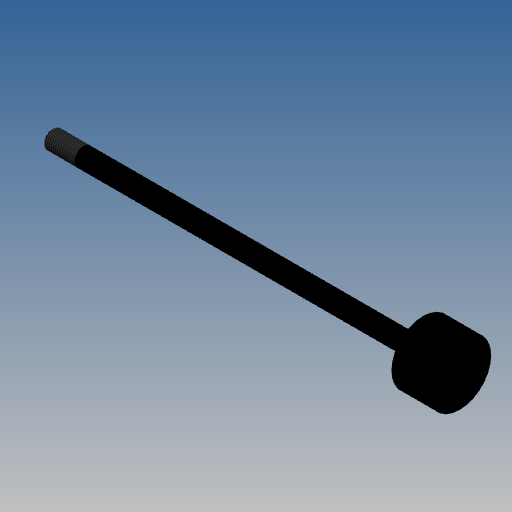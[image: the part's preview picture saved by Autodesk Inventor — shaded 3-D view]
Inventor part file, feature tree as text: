
AUTODESK INVENTOR PART (.ipt)
format: ipt  version: 2020 (Build 240168000, 168)  size: 157,184 bytes
history: native  units: in
note: dims shown in document units (in); Inventor stores cm internally (conversion verified against a paired STEP export)
features: other x98, sketch x3, revolve x2, thread x1, extrude x1
ambient origin geometry x8: Origin, YZ Plane, XZ Plane, XY Plane, X Axis, Y Axis, Z Axis, Center Point
bodies: Solid1 (feature_tree)
feature tree (105):
  revolve  "Revolution1"  Angle=360.0deg
  revolve  "Revolution2"  [1 undecoded]
  thread  "Thread1"  [1 undecoded]
  extrude  "Extrusion1"  [1 undecoded]
  other  "dia1_XY"
  other  "dia1_YZ"
  other  "dia1_ZX"
  other  "dia1_X"
  other  "dia1_Y"
  other  "dia1_Z"
  other  "dia1_Center"
  other  "dia12_XY"
  other  "dia12_YZ"
  other  "dia12_ZX"
  other  "dia12_X"
  other  "dia12_Y"
  other  "dia12_Z"
  other  "dia12_Center"
  other  "dia2_XY"
  other  "dia2_YZ"
  other  "dia2_ZX"
  other  "dia2_X"
  other  "dia2_Y"
  other  "dia2_Z"
  other  "dia2_Center"
  other  "dia22_XY"
  other  "dia22_YZ"
  other  "dia22_ZX"
  other  "dia22_X"
  other  "dia22_Y"
  other  "dia22_Z"
  other  "dia22_Center"
  other  "rl1_XY"
  other  "rl1_YZ"
  other  "rl1_ZX"
  other  "rl1_X"
  other  "rl1_Y"
  other  "rl1_Z"
  other  "rl1_Center"
  other  "rl2_XY"
  other  "rl2_YZ"
  other  "rl2_ZX"
  other  "rl2_X"
  other  "rl2_Y"
  other  "rl2_Z"
  other  "rl2_Center"
  other  "rod_cp_XY"
  other  "rod_cp_YZ"
  other  "rod_cp_ZX"
  other  "rod_cp_X"
  other  "rod_cp_Y"
  other  "rod_cp_Z"
  other  "rod_cp_Center"
  other  "thd1_XY"
  other  "thd1_YZ"
  other  "thd1_ZX"
  other  "thd1_X"
  other  "thd1_Y"
  other  "thd1_Z"
  other  "thd1_Center"
  other  "thd2_XY"
  other  "thd2_YZ"
  other  "thd2_ZX"
  other  "thd2_X"
  other  "thd2_Y"
  other  "thd2_Z"
  other  "thd2_Center"
  other  "to_rod_clevis_XY"
  other  "to_rod_clevis_YZ"
  other  "to_rod_clevis_ZX"
  other  "to_rod_clevis_X"
  other  "to_rod_clevis_Y"
  other  "to_rod_clevis_Z"
  other  "to_rod_clevis_Center"
  other  "wf1_XY"
  other  "wf1_YZ"
  other  "wf1_ZX"
  other  "wf1_X"
  other  "wf1_Y"
  other  "wf1_Z"
  other  "wf1_Center"
  other  "wf2_XY"
  other  "wf2_YZ"
  other  "wf2_ZX"
  other  "wf2_X"
  other  "wf2_Y"
  other  "wf2_Z"
  other  "wf2_Center"
  other  "wfw1_XY"
  other  "wfw1_YZ"
  other  "wfw1_ZX"
  other  "wfw1_X"
  other  "wfw1_Y"
  other  "wfw1_Z"
  other  "wfw1_Center"
  other  "wfw2_XY"
  other  "wfw2_YZ"
  other  "wfw2_ZX"
  other  "wfw2_X"
  other  "wfw2_Y"
  other  "wfw2_Z"
  other  "wfw2_Center"
  sketch  "Sketch_1"  dims[d0=360.0deg d1=360.0deg]
  sketch  "Sketch_3"  dims[d2=0.7203in d3=0.0in d4=0.25in d5=0.0in]
  sketch  "Sketch_10"  dims[d6=0.0in d7=0.0in d8=0.0in d9=0.0in d10=0.0in d11=0.0in d12=0.0in]
note: 3 required parameter values undecoded (feature->parameter linkage not recoverable at this tier; creation-order binding heuristic only, values carry confidence <= 0.55)